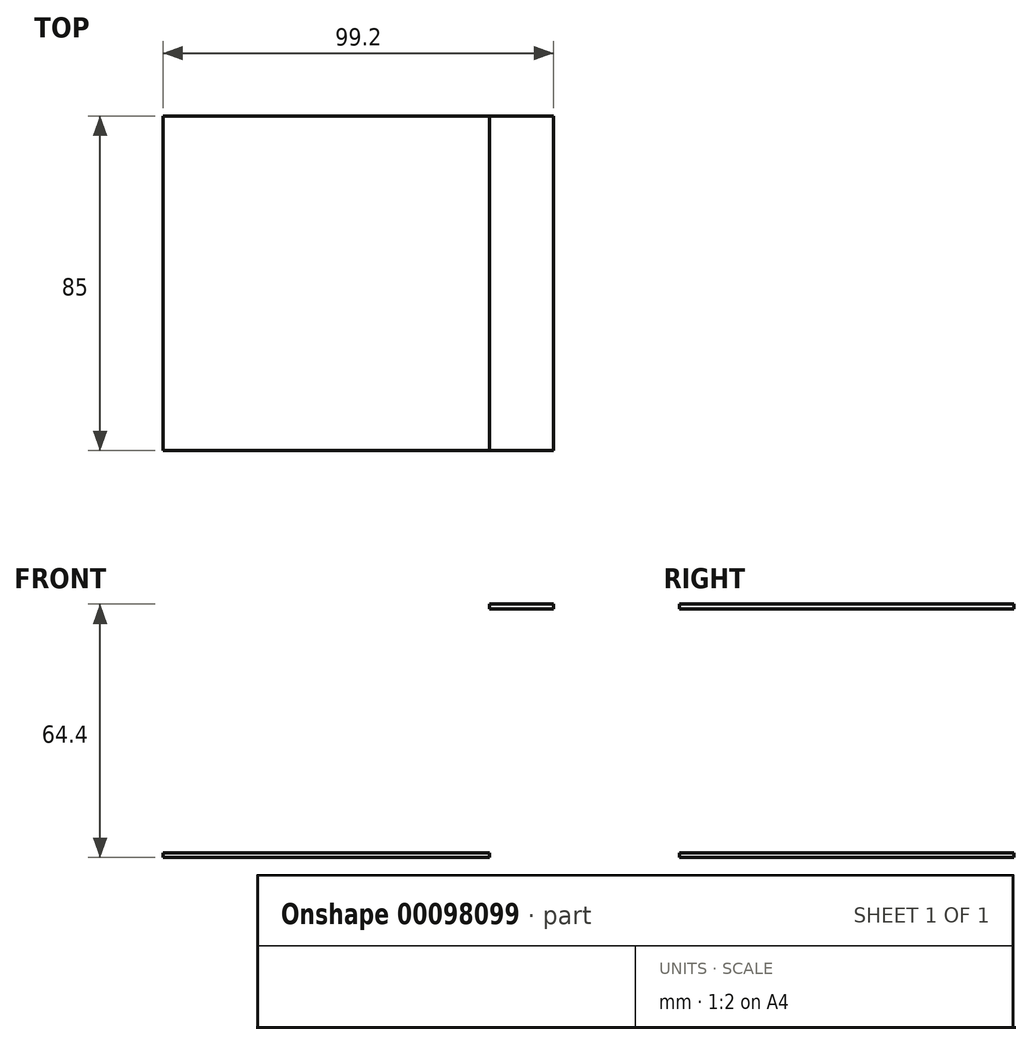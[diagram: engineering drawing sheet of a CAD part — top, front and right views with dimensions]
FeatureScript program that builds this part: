
annotation { "Feature Type Name" : "Feature", "Feature Type Description" : "" }
export const myFeature = defineFeature(function(context is Context, id is Id, definition is map)
    precondition{}
    {
        {
            var Q0;
            Q0=qCreatedBy(makeId("Front.planeOp"),FACE);
            var sketch = newSketch(context, id + "F0", { "sketchPlane" : qUnion([Q0])});
            skLineSegment(sketch, "E0.bottom", {"start": v(0, 0) * mm, "end": v(83, 0) * mm});
            skLineSegment(sketch, "E0.top", {"start": v(0, -23) * mm, "end": v(83, -23) * mm});
            skLineSegment(sketch, "E0.left", {"start": v(0, 0) * mm, "end": v(0, -23) * mm});
            skLineSegment(sketch, "E0.right", {"start": v(83, 0) * mm, "end": v(83, -23) * mm});
            skLineSegment(sketch, "E1.bottom", {"start": v(83, 39) * mm, "end": v(98, 39) * mm});
            skLineSegment(sketch, "E1.top", {"start": v(83, -11.5) * mm, "end": v(98, -11.5) * mm});
            skLineSegment(sketch, "E1.left", {"start": v(83, 39) * mm, "end": v(83, -11.5) * mm});
            skLineSegment(sketch, "E1.right", {"start": v(98, 39) * mm, "end": v(98, -11.5) * mm});
            skSolve(sketch);
        }
        {
            var Q0;
            Q0 = qSketchRegion(id + "F0", true);
            extrude(context, id + "F1", {"entities" : qUnion([Q0]), "endBound" : BoundingType.SYMMETRIC, "depth" : 67 * mm});
        }
        {
            var Q0;
            Q0=qCreatedBy(makeId("Front.planeOp"),FACE);
            var sketch = newSketch(context, id + "F2", { "sketchPlane" : qUnion([Q0])});
            skLineSegment(sketch, "E2.0.0", {"start": v(83, 0) * mm, "end": v(0, 0) * mm});
            skLineSegment(sketch, "E2.0.1", {"start": v(0, 0) * mm, "end": v(0, -23) * mm});
            skLineSegment(sketch, "E2.0.2", {"start": v(0, -23) * mm, "end": v(83, -23) * mm});
            skLineSegment(sketch, "E2.0.3", {"start": v(83, -23) * mm, "end": v(83, -11.5) * mm});
            skLineSegment(sketch, "E2.0.4", {"start": v(83, -11.5) * mm, "end": v(98, -11.5) * mm});
            skLineSegment(sketch, "E2.0.5", {"start": v(98, -11.5) * mm, "end": v(98, 39) * mm});
            skLineSegment(sketch, "E2.0.6", {"start": v(98, 39) * mm, "end": v(83, 39) * mm});
            skLineSegment(sketch, "E2.0.7", {"start": v(83, 39) * mm, "end": v(83, 0) * mm});
            skLineSegment(sketch, "E3.bottom", {"start": v(83, 39) * mm, "end": v(99.2, 39) * mm});
            skLineSegment(sketch, "E3.top", {"start": v(83, 40.2) * mm, "end": v(99.2, 40.2) * mm});
            skLineSegment(sketch, "E3.left", {"start": v(83, 39) * mm, "end": v(83, 40.2) * mm});
            skLineSegment(sketch, "E3.right", {"start": v(99.2, 39) * mm, "end": v(99.2, 40.2) * mm});
            skLineSegment(sketch, "E4.bottom", {"start": v(99.2, 39) * mm, "end": v(98, 39) * mm});
            skLineSegment(sketch, "E4.top", {"start": v(99.2, -12.7) * mm, "end": v(98, -12.7) * mm});
            skLineSegment(sketch, "E4.left", {"start": v(99.2, 39) * mm, "end": v(99.2, -12.7) * mm});
            skLineSegment(sketch, "E4.right", {"start": v(98, 39) * mm, "end": v(98, -12.7) * mm});
            skLineSegment(sketch, "E5.bottom", {"start": v(98, -11.5) * mm, "end": v(83, -11.5) * mm});
            skLineSegment(sketch, "E5.top", {"start": v(98, -12.7) * mm, "end": v(83, -12.7) * mm});
            skLineSegment(sketch, "E5.left", {"start": v(98, -11.5) * mm, "end": v(98, -12.7) * mm});
            skLineSegment(sketch, "E5.right", {"start": v(83, -11.5) * mm, "end": v(83, -12.7) * mm});
            skLineSegment(sketch, "E6.bottom", {"start": v(84.2, -12.7) * mm, "end": v(83, -12.7) * mm});
            skLineSegment(sketch, "E6.top", {"start": v(84.2, -24.2) * mm, "end": v(83, -24.2) * mm});
            skLineSegment(sketch, "E6.left", {"start": v(84.2, -12.7) * mm, "end": v(84.2, -24.2) * mm});
            skLineSegment(sketch, "E6.right", {"start": v(83, -12.7) * mm, "end": v(83, -24.2) * mm});
            skLineSegment(sketch, "E7.bottom", {"start": v(83, -24.2) * mm, "end": v(0, -24.2) * mm});
            skLineSegment(sketch, "E7.top", {"start": v(83, -23) * mm, "end": v(0, -23) * mm});
            skLineSegment(sketch, "E7.left", {"start": v(83, -24.2) * mm, "end": v(83, -23) * mm});
            skLineSegment(sketch, "E7.right", {"start": v(0, -24.2) * mm, "end": v(0, -23) * mm});
            skSolve(sketch);
        }
        {
            var Q0;
            Q0=makeQuery(id+"F2.imprint","IMPRINT",FACE,{"disambiguationData":[TD([[makeQuery(id+"F2.imprint","IMPRINT",EDGE,{"derivedFrom":sQuery(id+"F2.wireOp",EDGE,"E3.bottom")}),1.0]])]});
            var Q1;
            Q1=makeQuery(id+"F2.imprint","IMPRINT",FACE,{"disambiguationData":[TD([[makeQuery(id+"F2.imprint","IMPRINT",EDGE,{"derivedFrom":sQuery(id+"F2.wireOp",EDGE,"E4.bottom")}),1.0]])]});
            var Q2;
            Q2=makeQuery(id+"F2.imprint","IMPRINT",FACE,{"disambiguationData":[TD([[makeQuery(id+"F2.imprint","IMPRINT",EDGE,{"derivedFrom":sQuery(id+"F2.wireOp",EDGE,"E7.bottom")}),-1.0]])]});
            var Q3;
            Q3=makeQuery(id+"F2.imprint","IMPRINT",FACE,{"disambiguationData":[TD([[makeQuery(id+"F2.imprint","IMPRINT",EDGE,{"derivedFrom":sQuery(id+"F2.wireOp",EDGE,"E6.bottom")}),1.0]])]});
            var Q4;
            Q4=makeQuery(id+"F2.imprint","IMPRINT",FACE,{"disambiguationData":[TD([[makeQuery(id+"F2.imprint","IMPRINT",EDGE,{"derivedFrom":sQuery(id+"F2.wireOp",EDGE,"E5.bottom")}),1.0]])]});
            extrude(context, id + "F3", {"entities" : qUnion([Q0, Q1, Q2, Q3, Q4]), "operationType" : NewBodyOperationType.ADD, "endBound" : BoundingType.SYMMETRIC, "depth" : 85 * mm});
        }
        {
            var Q0;
            Q0=makeQuery(id+"F1.opExtrude","CAP_FACE",FACE,{"disambiguationData":[OSD([sQuery(id+"F0.wireOp",EDGE,"E0.bottom"),sQuery(id+"F0.wireOp",EDGE,"E0.top"),sQuery(id+"F0.wireOp",EDGE,"E0.left"),sQuery(id+"F0.wireOp",EDGE,"E0.right"),sQuery(id+"F0.wireOp",EDGE,"E1.bottom"),sQuery(id+"F0.wireOp",EDGE,"E1.top"),sQuery(id+"F0.wireOp",EDGE,"E1.left"),sQuery(id+"F0.wireOp",EDGE,"E1.right")])],"isStart":false});
            var sketch = newSketch(context, id + "F4", { "sketchPlane" : qUnion([Q0])});
            skLineSegment(sketch, "E8.0", {"start": v(85, 37) * mm, "end": v(85, -2) * mm});
            skLineSegment(sketch, "E8.1", {"start": v(96, 37) * mm, "end": v(85, 37) * mm});
            skLineSegment(sketch, "E8.2", {"start": v(85, -2) * mm, "end": v(2, -2) * mm});
            skLineSegment(sketch, "E8.3", {"start": v(96, -9.5) * mm, "end": v(96, 37) * mm});
            skLineSegment(sketch, "E8.4", {"start": v(2, -2) * mm, "end": v(2, -21) * mm});
            skLineSegment(sketch, "E8.5", {"start": v(2, -21) * mm, "end": v(81, -21) * mm});
            skLineSegment(sketch, "E8.6", {"start": v(81, -21) * mm, "end": v(81, -9.5) * mm});
            skLineSegment(sketch, "E8.7", {"start": v(81, -9.5) * mm, "end": v(96, -9.5) * mm});
            skLineSegment(sketch, "E9", {"start": v(2, -2) * mm, "end": v(21, -21) * mm});
            skLineSegment(sketch, "E10", {"start": v(21.85, -20.15) * mm, "end": v(40, -2) * mm});
            skLineSegment(sketch, "E11", {"start": v(40.85, -2.85) * mm, "end": v(59, -21) * mm});
            skLineSegment(sketch, "E12", {"start": v(59.85, -20.15) * mm, "end": v(78, -2) * mm});
            skLineSegment(sketch, "E13", {"start": v(78.85, -2.85) * mm, "end": v(85.5, -9.5) * mm});
            skLineSegment(sketch, "E14", {"start": v(96, 4) * mm, "end": v(85.85, 14.15) * mm});
            skLineSegment(sketch, "E15", {"start": v(85, 15) * mm, "end": v(95.15, 25.15) * mm});
            skLineSegment(sketch, "E16", {"start": v(96, 26) * mm, "end": v(85, 37) * mm});
            skLineSegment(sketch, "E17", {"start": v(86.29, -8.79) * mm, "end": v(96, 0) * mm});
            skLineSegment(sketch, "E18", {"start": v(3.7, -2) * mm, "end": v(21.85, -20.15) * mm});
            skLineSegment(sketch, "E19", {"start": v(40.85, -2.85) * mm, "end": v(22.7, -21) * mm});
            skLineSegment(sketch, "E20", {"start": v(41.7, -2) * mm, "end": v(59.85, -20.15) * mm});
            skLineSegment(sketch, "E21", {"start": v(78.85, -2.85) * mm, "end": v(60.7, -21) * mm});
            skLineSegment(sketch, "E22", {"start": v(79.5, -2) * mm, "end": v(85.44, -7.94) * mm});
            skLineSegment(sketch, "E23", {"start": v(85.44, -7.94) * mm, "end": v(96, 1.62) * mm});
            skLineSegment(sketch, "E24", {"start": v(85, 13.3) * mm, "end": v(96, 2.3) * mm});
            skLineSegment(sketch, "E25", {"start": v(85.85, 14.15) * mm, "end": v(96, 24.3) * mm});
            skLineSegment(sketch, "E26", {"start": v(95.15, 25.15) * mm, "end": v(85, 35.3) * mm});
            skLineSegment(sketch, "E27.trimOffspring", {"start": v(86.29, -8.79) * mm, "end": v(87, -9.5) * mm});
            skSolve(sketch);
        }
        {
            var Q0;
            {var subQ0=sQuery(id+"F4.wireOp",EDGE,"E8.4");Q0=makeQuery(id+"F4.imprint","IMPRINT",FACE,{"disambiguationData":[TD([[makeQuery(id+"F4.imprint","IMPRINT",EDGE,{"derivedFrom":subQ0}),1.0]])]});}
            var Q1;
            {var subQ0=sQuery(id+"F4.wireOp",EDGE,"E10");Q1=makeQuery(id+"F4.imprint","IMPRINT",FACE,{"disambiguationData":[TD([[makeQuery(id+"F4.imprint","IMPRINT",EDGE,{"derivedFrom":subQ0}),1.0]])]});}
            var Q2;
            {var subQ0=sQuery(id+"F4.wireOp",EDGE,"E11");Q2=makeQuery(id+"F4.imprint","IMPRINT",FACE,{"disambiguationData":[TD([[makeQuery(id+"F4.imprint","IMPRINT",EDGE,{"derivedFrom":subQ0}),-1.0]])]});}
            var Q3;
            {var subQ0=sQuery(id+"F4.wireOp",EDGE,"E12");Q3=makeQuery(id+"F4.imprint","IMPRINT",FACE,{"disambiguationData":[TD([[makeQuery(id+"F4.imprint","IMPRINT",EDGE,{"derivedFrom":subQ0}),1.0]])]});}
            var Q4;
            {var subQ2=sQuery(id+"F4.wireOp",EDGE,"E8.6");Q4=makeQuery(id+"F4.imprint","IMPRINT",FACE,{"disambiguationData":[TD([[makeQuery(id+"F4.imprint","IMPRINT",EDGE,{"derivedFrom":subQ2}),1.0]])]});}
            var Q5;
            {var subQ3=sQuery(id+"F4.wireOp",EDGE,"E17");Q5=makeQuery(id+"F4.imprint","IMPRINT",FACE,{"disambiguationData":[TD([[makeQuery(id+"F4.imprint","IMPRINT",EDGE,{"derivedFrom":subQ3}),-1.0]])]});}
            var Q6;
            {var subQ0=sQuery(id+"F4.wireOp",EDGE,"E22");Q6=makeQuery(id+"F4.imprint","IMPRINT",FACE,{"disambiguationData":[TD([[makeQuery(id+"F4.imprint","IMPRINT",EDGE,{"derivedFrom":subQ0}),1.0]])]});}
            var Q7;
            {var subQ0=sQuery(id+"F4.wireOp",EDGE,"E14");Q7=makeQuery(id+"F4.imprint","IMPRINT",FACE,{"disambiguationData":[TD([[makeQuery(id+"F4.imprint","IMPRINT",EDGE,{"derivedFrom":subQ0}),-1.0]])]});}
            var Q8;
            {var subQ0=sQuery(id+"F4.wireOp",EDGE,"E15");Q8=makeQuery(id+"F4.imprint","IMPRINT",FACE,{"disambiguationData":[TD([[makeQuery(id+"F4.imprint","IMPRINT",EDGE,{"derivedFrom":subQ0}),1.0]])]});}
            var Q9;
            {var subQ0=sQuery(id+"F4.wireOp",EDGE,"E8.1");Q9=makeQuery(id+"F4.imprint","IMPRINT",FACE,{"disambiguationData":[TD([[makeQuery(id+"F4.imprint","IMPRINT",EDGE,{"derivedFrom":subQ0}),1.0]])]});}
            extrude(context, id + "F5", {"entities" : qUnion([Q0, Q1, Q2, Q3, Q4, Q5, Q6, Q7, Q8, Q9]), "operationType" : NewBodyOperationType.REMOVE, "endBound" : BoundingType.THROUGH_ALL, "oppositeDirection" : true, "depth" : 25 * mm});
        }
        {
            var Q0;
            Q0=makeQuery(id+"F1.opExtrude","CAP_FACE",FACE,{"disambiguationData":[OSD([sQuery(id+"F0.wireOp",EDGE,"E0.bottom"),sQuery(id+"F0.wireOp",EDGE,"E0.top"),sQuery(id+"F0.wireOp",EDGE,"E0.left"),sQuery(id+"F0.wireOp",EDGE,"E0.right"),sQuery(id+"F0.wireOp",EDGE,"E1.bottom"),sQuery(id+"F0.wireOp",EDGE,"E1.top"),sQuery(id+"F0.wireOp",EDGE,"E1.left"),sQuery(id+"F0.wireOp",EDGE,"E1.right")])],"isStart":false});
            var sketch = newSketch(context, id + "F6", { "sketchPlane" : qUnion([Q0])});
            skLineSegment(sketch, "E28.0.0", {"start": v(83, 0) * mm, "end": v(0, 0) * mm});
            skLineSegment(sketch, "E28.0.1", {"start": v(0, 0) * mm, "end": v(0, -23) * mm});
            skLineSegment(sketch, "E28.0.2", {"start": v(0, -23) * mm, "end": v(83, -23) * mm});
            skLineSegment(sketch, "E28.0.3", {"start": v(83, -23) * mm, "end": v(83, -11.5) * mm});
            skLineSegment(sketch, "E28.0.4", {"start": v(83, -11.5) * mm, "end": v(98, -11.5) * mm});
            skLineSegment(sketch, "E28.0.5", {"start": v(98, -11.5) * mm, "end": v(98, 39) * mm});
            skLineSegment(sketch, "E28.0.6", {"start": v(98, 39) * mm, "end": v(83, 39) * mm});
            skLineSegment(sketch, "E28.0.7", {"start": v(83, 39) * mm, "end": v(83, 0) * mm});
            skSolve(sketch);
        }
        {
            var Q0;
            Q0 = qSketchRegion(id + "F6", true);
            extrude(context, id + "F7", {"entities" : qUnion([Q0]), "operationType" : NewBodyOperationType.REMOVE, "endBound" : BoundingType.THROUGH_ALL, "oppositeDirection" : true, "depth" : 25 * mm});
        }
    });
